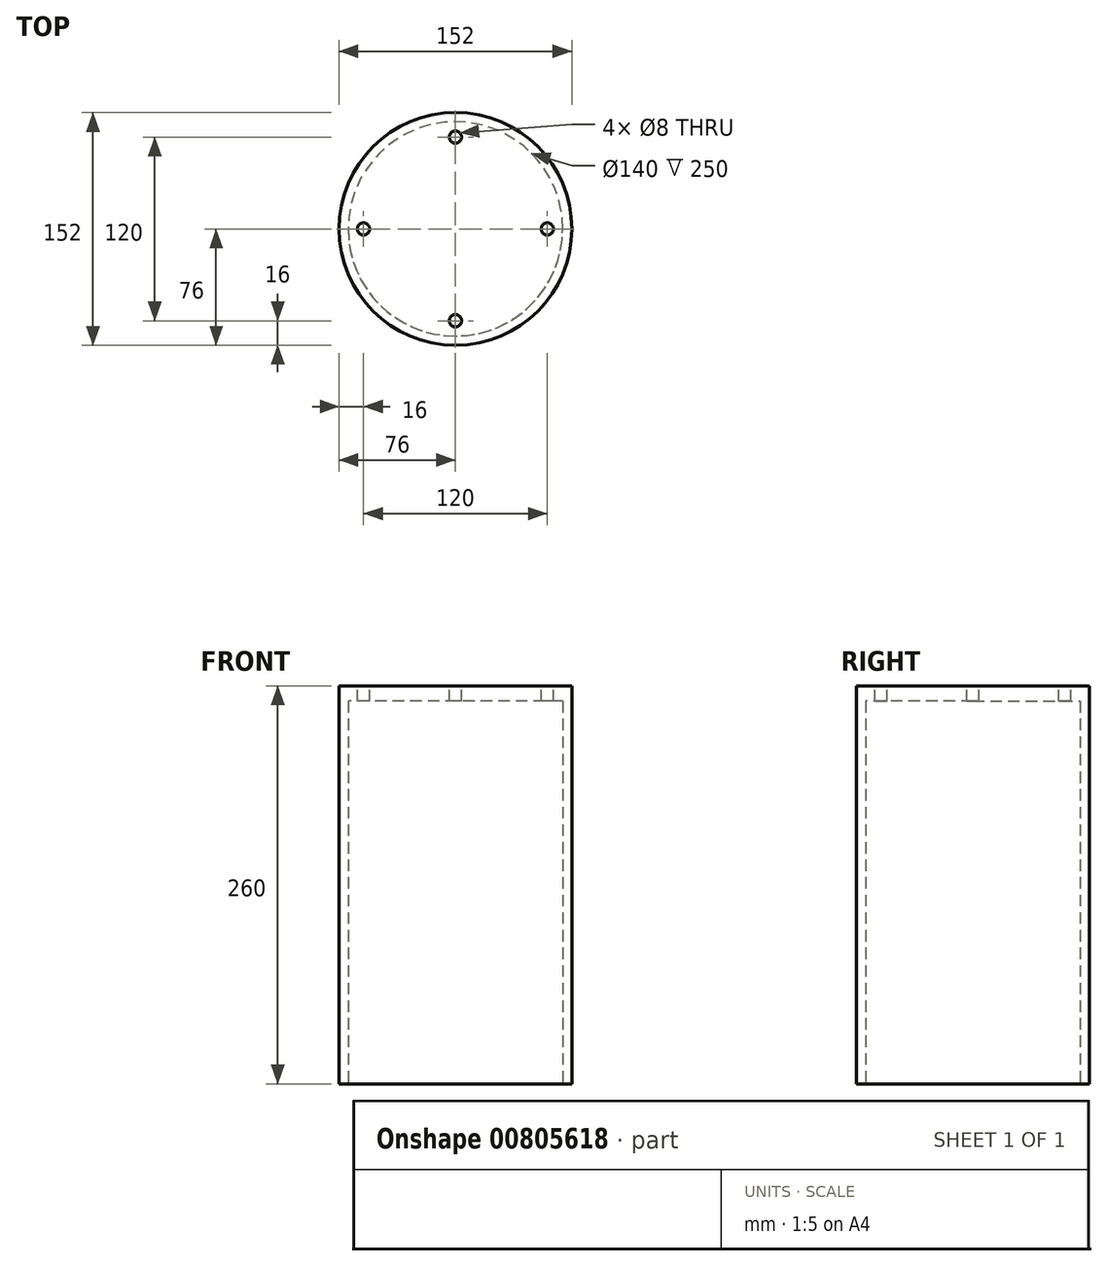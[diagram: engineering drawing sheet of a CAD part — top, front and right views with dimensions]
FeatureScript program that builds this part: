
annotation { "Feature Type Name" : "Feature", "Feature Type Description" : "" }
export const myFeature = defineFeature(function(context is Context, id is Id, definition is map)
    precondition{}
    {
        {
            var Q0;
            Q0=qCreatedBy(makeId("Top.planeOp"),FACE);
            var sketch = newSketch(context, id + "F0", { "sketchPlane" : qUnion([Q0])});
            skCircle(sketch, "E0", {"center": v(0, 0) * mm, "radius": 76 * mm});
            skSolve(sketch);
        }
        {
            var Q0;
            Q0=makeQuery(id+"F0.imprint","IMPRINT",FACE,{"disambiguationData":[TD([[makeQuery(id+"F0.imprint","IMPRINT",EDGE,{"derivedFrom":sQuery(id+"F0.wireOp",EDGE,"E0")}),1.0]])]});
            extrude(context, id + "F1", {"entities" : qUnion([Q0]), "depth" : 10 * mm, "offsetDistance" : 25 * mm});
        }
        {
            var Q0;
            Q0=makeQuery(id+"F1.opExtrude","CAP_FACE",FACE,{"disambiguationData":[OSD([sQuery(id+"F0.wireOp",EDGE,"E0")])],"isStart":false});
            var sketch = newSketch(context, id + "F2", { "sketchPlane" : qUnion([Q0])});
            skCircle(sketch, "E1", {"center": v(-60, 0) * mm, "radius": 4 * mm});
            skCircle(sketch, "E2", {"center": v(60, 0) * mm, "radius": 4 * mm});
            skCircle(sketch, "E3", {"center": v(0, -60) * mm, "radius": 4 * mm});
            skCircle(sketch, "E4", {"center": v(0, 60) * mm, "radius": 4 * mm});
            skSolve(sketch);
        }
        {
            var Q0;
            Q0 = qSketchRegion(id + "F2", true);
            var Q1;
            Q1 = qConstructionFilter(qBodyType(qCreatedBy(id + "F2" ,EDGE), BodyType.WIRE), ConstructionObject.NO);
            var Q2;
            Q2=makeQuery(id+"F1.opExtrude","CAP_FACE",FACE,{"disambiguationData":[OSD([sQuery(id+"F0.wireOp",EDGE,"E0")])],"isStart":true});
            extrude(context, id + "F3", {"entities" : qUnion([Q0]), "operationType" : NewBodyOperationType.REMOVE, "surfaceEntities" : qUnion([Q1]), "endBound" : BoundingType.UP_TO_SURFACE, "oppositeDirection" : true, "depth" : 25 * mm, "endBoundEntityFace" : qUnion([Q2]), "offsetDistance" : 25 * mm});
        }
        {
            var Q0;
            Q0=makeQuery(id+"F1.opExtrude","CAP_FACE",FACE,{"disambiguationData":[OSD([sQuery(id+"F0.wireOp",EDGE,"E0")])],"isStart":true});
            extrude(context, id + "F4", {"entities" : qUnion([Q0]), "operationType" : NewBodyOperationType.ADD, "depth" : 250 * mm, "offsetDistance" : 25 * mm});
        }
        {
            var Q0;
            Q0=makeQuery(id+"F4.opExtrude","CAP_FACE",FACE,{"disambiguationData":[OSD([sQuery(id+"F0.wireOp",EDGE,"E0")])],"isStart":false});
            var sketch = newSketch(context, id + "F5", { "sketchPlane" : qUnion([Q0])});
            skCircle(sketch, "E5", {"center": v(0, 0) * mm, "radius": 70 * mm});
            skSolve(sketch);
        }
        {
            var Q0;
            Q0 = qSketchRegion(id + "F5", true);
            var Q1;
            Q1=makeQuery(id+"F1.opExtrude","CAP_FACE",FACE,{"disambiguationData":[OSD([sQuery(id+"F0.wireOp",EDGE,"E0")])],"isStart":false});
            extrude(context, id + "F6", {"entities" : qUnion([Q0]), "operationType" : NewBodyOperationType.REMOVE, "endBound" : BoundingType.UP_TO_SURFACE, "oppositeDirection" : true, "depth" : 200 * mm, "endBoundEntityFace" : qUnion([Q1]), "hasOffset" : true, "offsetDistance" : 10 * mm});
        }
    });
